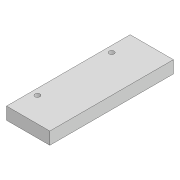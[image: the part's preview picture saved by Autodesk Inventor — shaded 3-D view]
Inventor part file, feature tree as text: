
AUTODESK INVENTOR PART (.ipt)
format: ipt  version: 2022 (Build 260153000, 153)  size: 90,624 bytes
history: native  units: mm
features: sketch x2, other x1, extrude x1, hole x1
ambient origin geometry x8: Origin, YZ Plane, XZ Plane, XY Plane, X Axis, Y Axis, Z Axis, Center Point
bodies: Body1 (feature_tree)
feature tree (5):
  other  "Твердое тело1"
  extrude  "Выдавливание1"  Depth=70.0mm
  hole  "Отверстие1"  [1 undecoded]
  sketch  "Эскиз1"
  sketch  "Эскиз2"
note: 1 required parameter value undecoded (feature->parameter linkage not recoverable at this tier; creation-order binding heuristic only, values carry confidence <= 0.55)
